# Revit family: 2015_Ventana_Alueuropa_Q77_1-Hoja_Fija
name_source: partatom
category: Windows
revit_build: Autodesk Revit 2015 (Build: 20140223_1515(x64)
units: mm (PartAtom-declared; Revit-internal decimal feet)

## types (1)
- 600x1000 mm
    AcidificacionAtmosferica = 0
    AcidificacionAtmosfericaPorUnidad = 0
    Acristalamiento = Cristal - Vidrio claro templado
    AguaConsumida = 0
    AguaConsumidaPorUnidad = 0
    Altura Máxima = 5000 mm  [stored 16.4042 ft]
    Altura Real = 1000 mm  [stored 3.28084 ft]
    Altura de antepecho por defecto = 800 mm
    Anchura Máxima = 5000 mm  [stored 16.4042 ft]
    Anchura Real = 600 mm  [stored 1.9685 ft]
    Area = 600000 mm²
    Autor = Bimetica Parametric Design Services, S.L.
    Bimetica = http://www.bimetica.com
    CambioClimatico = 0
    CambioClimaticoPorUnidad = 0
    CerramientoExterior = Yes
    ConfiguracionPoliamidas = 273800 - 493700
    ControlHumos = No
    CosteEnergeticoKwh = 0
    CosteEnergeticoMj = 0 J
    CosteMantenimiento = 0
    Description = Ventana Fija
    Desfase Acristalamiento = 5.25 mm  [stored 0.0172244 ft]
    DestruccionCapaOzonoEstratosferica = 0
    DestruccionCapaOzonoEstratosfericaPorUnidad = 0
    Detalle Perfileria = Yes
    EmisionCO2 = 0
    EnergiaNoRenovableConsumida = 0
    EnergiaNoRenovableConsumidaPorUnidad = 0
    EnergiaPrimariaTotalConsumida = 0
    EnergiaPrimariaTotalConsumidaPorUnidad = 0
    EnergiaRenovableConsumida = 0
    EnergiaRenovableConsumidaPorUnidad = 0
    Eutrofizacion = 0
    EutrofizacionPorUnidad = 0
    FactorSolarModificado = 3000000
    FactorSombra = 0
    FaltaDeRecursos = 0
    FaltaDeRecursosPorUnidad = 0
    FechaEmisionElementoBIM = 28/08/2016
    FechaVencimientoElementoBIM = 28/08/2017
    FormacionFotoquimicaOzono = 0
    FormacionFotoquimicaOzonoPorUnidad = 0
    FraccionAreaAcristalamiento = 0.00%
    GrosorAcristalamiento = 32 mm  [stored 0.104987 ft]
    GrosorMarco = 70 mm  [stored 0.229659 ft]
    Height = 1000 mm  [stored 3.28084 ft]
    InformacionTecnica = http://www.alueuropa.com
    Manufacturer = Alueuropa
    Marco = Aluminio
    MasaSuperficialKgm2 = 0
    MasterformatCodigo = 08 51 13
    MasterformatTitulo = Aluminium Windows
    MateriaPrima = 0
    Model = Q77 Fija
    Motorizada = No
    OmniclassCodigo = 23.30.20.17.21.21
    OmniclassTitulo = Casment Window
    Operation = Fija
    Perimetro = 3200
    Poliamida = Poliamida, Technoform Bautec, PA66 GF 25
    ReferenciaContacto = Alueuropa
    RepisaExterior = Yes
    RepisaInterior = Yes
    ResiduoInerte = 0
    ResiduoInertePorUnidad = 0
    ResiduoRadioactivo = 0
    ResiduoRadioactivoPorUnidad = 0
    ResiduosNoPeligrosos = 0
    ResiduosNoPeligrososPorUnidad = 0
    ResiduosPeligrosos = 0
    ResiduosPeligrososPorUnidad = 0
    Rough Height = 605 mm
    Rough Width = 1005 mm  [stored 3.29724 ft]
    SalidaEmergencia = No
    TelefonoContacto = +34 91 8955800
    TransmitanciaTermica = 0 W/(m²·K)
    Type Comments = Sistema de Ventana Q77  Fija
    UNSPSCCodigo = 30171600
    UNSPSCTitulo = Windows
    URL = http://www.alueuropa.com
    URL Poliamida = http://www.technoform.es
    URL Poliamida - Catálogo = http://www.technoform.com
    URLProducto = http://www.alueuropa.com
    Uniclass2.0Codigo = 25-30
    Uniclass2.0Titulo = Door and window systems
    VersionElementoBIM = 1.0
    Wall Closure = By host
    Width = 600 mm  [stored 1.9685 ft]
    Y𝑔 = 0.11
    𝐴𝑓 = 150000
    𝐴𝑔 = 450000
    𝑈𝑓 = 3.629
    𝑈𝑔 = 1.9
    𝑈𝑤 = 2.845583
    𝑙𝑔 = 2800

note: [stored X ft] marks values corroborated as IEEE doubles in the binary element streams (Revit-internal decimal feet)
